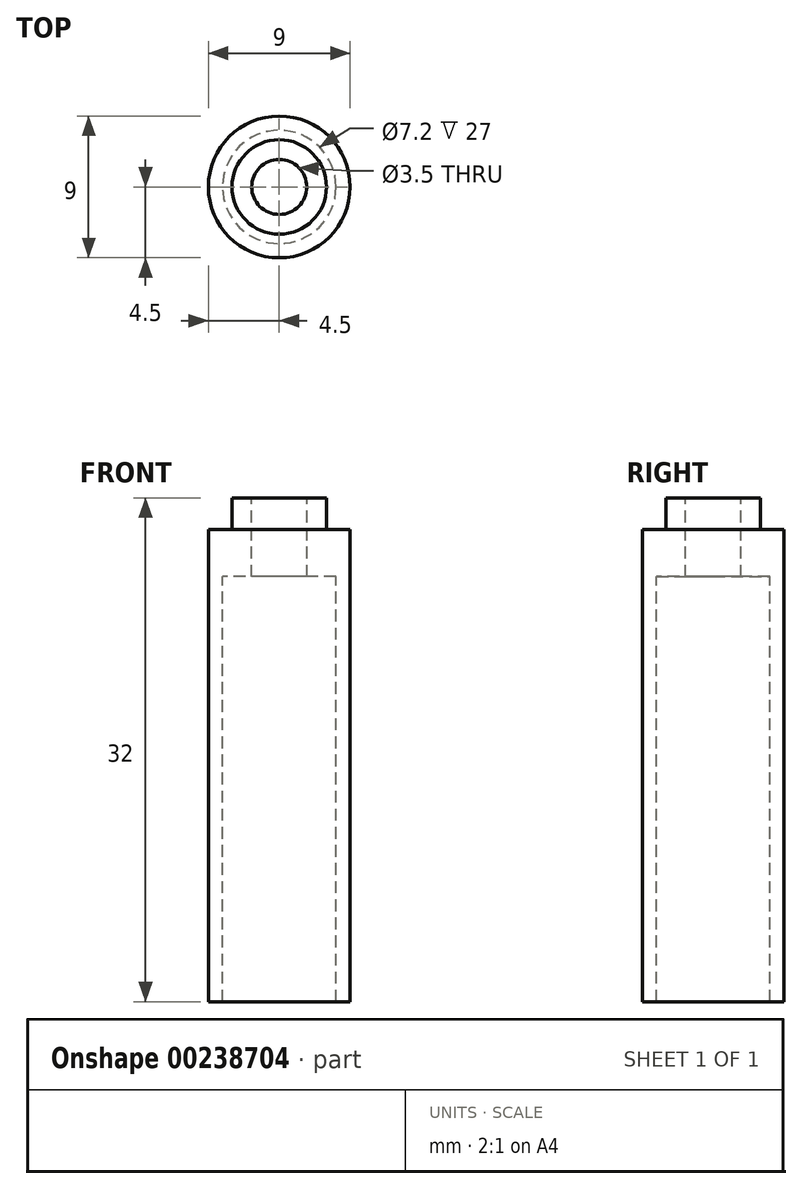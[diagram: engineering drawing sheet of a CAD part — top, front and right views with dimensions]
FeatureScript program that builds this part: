
annotation { "Feature Type Name" : "Feature", "Feature Type Description" : "" }
export const myFeature = defineFeature(function(context is Context, id is Id, definition is map)
    precondition{}
    {
        {
            var Q0;
            Q0=qCreatedBy(makeId("Top.planeOp"),FACE);
            var sketch = newSketch(context, id + "F0", { "sketchPlane" : qUnion([Q0])});
            skCircle(sketch, "E0", {"center": v(0, 0) * mm, "radius": 4.5 * mm});
            skCircle(sketch, "E1", {"center": v(0, 0) * mm, "radius": 3.6 * mm});
            skCircle(sketch, "E2", {"center": v(0, 0) * mm, "radius": 1.75 * mm});
            skCircle(sketch, "E3", {"center": v(0, 0) * mm, "radius": 3 * mm});
            skSolve(sketch);
        }
        {
            var Q0;
            Q0 = qSketchRegion(id + "F0", true);
            extrude(context, id + "F1", {"entities" : qUnion([Q0]), "oppositeDirection" : true, "depth" : 30 * mm});
        }
        {
            var Q0;
            Q0=makeQuery(id+"F0.imprint","IMPRINT",FACE,{"disambiguationData":[TD([[makeQuery(id+"F0.imprint","IMPRINT",EDGE,{"derivedFrom":sQuery(id+"F0.wireOp",EDGE,"E1")}),1.0]])]});
            var Q1;
            Q1=makeQuery(id+"F0.imprint","IMPRINT",FACE,{"disambiguationData":[TD([[makeQuery(id+"F0.imprint","IMPRINT",EDGE,{"derivedFrom":sQuery(id+"F0.wireOp",EDGE,"E2")}),-1.0]])]});
            extrude(context, id + "F2", {"entities" : qUnion([Q0, Q1]), "operationType" : NewBodyOperationType.ADD, "oppositeDirection" : true, "depth" : 3 * mm});
        }
        {
            var Q0;
            Q0=makeQuery(id+"F0.imprint","IMPRINT",FACE,{"disambiguationData":[TD([[makeQuery(id+"F0.imprint","IMPRINT",EDGE,{"derivedFrom":sQuery(id+"F0.wireOp",EDGE,"E2")}),-1.0]])]});
            extrude(context, id + "F3", {"entities" : qUnion([Q0]), "operationType" : NewBodyOperationType.ADD, "depth" : 2 * mm});
        }
    });
